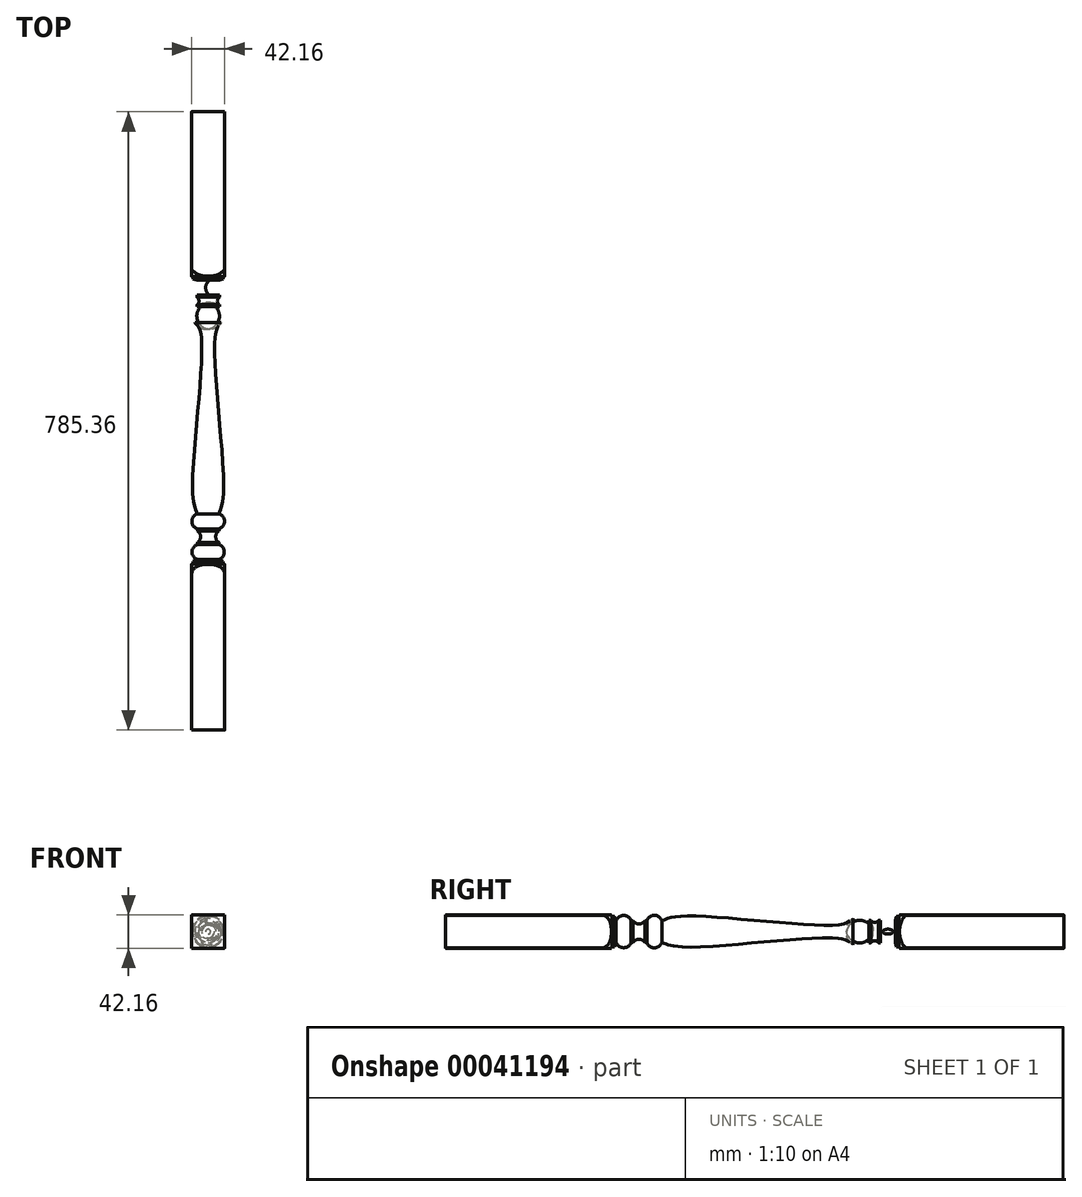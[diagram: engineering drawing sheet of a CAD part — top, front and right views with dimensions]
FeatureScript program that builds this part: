
annotation { "Feature Type Name" : "Feature", "Feature Type Description" : "" }
export const myFeature = defineFeature(function(context is Context, id is Id, definition is map)
    precondition{}
    {
        {
            var Q0;
            Q0=qCreatedBy(makeId("Right.planeOp"),FACE);
            var sketch = newSketch(context, id + "F0", { "sketchPlane" : qUnion([Q0])});
            skLineSegment(sketch, "E0", {"start": v(-252.74, 13.28) * mm, "end": v(-54.81, 13.28) * mm});
            skArc(sketch, "E1", {"start": v(-54.81, 13.28) * mm, "mid": v(-46.4, 16.2) * mm, "end": v(-41.6, 23.69) * mm});
            skLineSegment(sketch, "E2", {"start": v(-41.6, 23.69) * mm, "end": v(-38.43, 23.69) * mm});
            skLineSegment(sketch, "E3", {"start": v(-38.43, 23.69) * mm, "end": v(-36.14, 29.21) * mm});
            skArc(sketch, "E4", {"start": v(-36.14, 29.21) * mm, "mid": v(-26.62, 22.43) * mm, "end": v(-17.1, 29.21) * mm});
            skLineSegment(sketch, "E5", {"start": v(0.3, 29.21) * mm, "end": v(2.84, 29.21) * mm});
            skArc(sketch, "E6", {"start": v(2.84, 29.21) * mm, "mid": v(12.37, 22.22) * mm, "end": v(21.9, 29.21) * mm});
            skArc(sketch, "E7", {"start": v(264.65, 26.2) * mm, "mid": v(275.23, 23.95) * mm, "end": v(284.97, 28.64) * mm});
            skLineSegment(sketch, "E8", {"start": v(284.97, 28.64) * mm, "end": v(287.51, 28.64) * mm});
            skLineSegment(sketch, "E9", {"start": v(297.04, 28.64) * mm, "end": v(299.58, 28.64) * mm});
            skArc(sketch, "E10", {"start": v(299.58, 28.64) * mm, "mid": v(309.1, 23.44) * mm, "end": v(318.63, 28.64) * mm});
            skLineSegment(sketch, "E11", {"start": v(318.63, 28.64) * mm, "end": v(319.9, 23.69) * mm});
            skLineSegment(sketch, "E12", {"start": v(319.9, 23.69) * mm, "end": v(323.07, 23.69) * mm});
            skLineSegment(sketch, "E13", {"start": v(332.6, 13.28) * mm, "end": v(532.62, 13.28) * mm});
            skLineSegment(sketch, "E14", {"start": v(-252.74, 42.93) * mm, "end": v(636.26, 42.93) * mm, "construction": true});
            skLineSegment(sketch, "E15", {"start": v(-17.1, 29.21) * mm, "end": v(-14.55, 29.21) * mm});
            skArc(sketch, "E16", {"start": v(323.07, 23.69) * mm, "mid": v(326.67, 17.42) * mm, "end": v(332.6, 13.28) * mm});
            skLineSegment(sketch, "E17", {"start": v(38.25, 23.05) * mm, "end": v(191.9, 23.05) * mm, "construction": true});
            skFitSpline(sketch, "E18", {"points": [v(21.9, 29.21) * mm, v(52.9, 23.05) * mm, v(249.18, 33.93) * mm, v(264.65, 26.2) * mm], "startDerivative": vector(83.71, -33.8) * mm, "endDerivative": vector(63.68, -47.75) * mm});
            skLineSegment(sketch, "E19.0", {"start": v(-278.65, -33.84) * mm, "end": v(508.75, -33.84) * mm});
            skLineSegment(sketch, "E20", {"start": v(532.62, 13.28) * mm, "end": v(532.62, 42.93) * mm});
            skLineSegment(sketch, "E21", {"start": v(532.62, 42.93) * mm, "end": v(659.62, 42.93) * mm});
            skLineSegment(sketch, "E22", {"start": v(659.62, 42.93) * mm, "end": v(659.62, -33.84) * mm});
            skLineSegment(sketch, "E23", {"start": v(659.62, -33.84) * mm, "end": v(508.75, -33.84) * mm});
            skLineSegment(sketch, "E24", {"start": v(-252.74, 13.28) * mm, "end": v(-252.74, 42.93) * mm});
            skLineSegment(sketch, "E25", {"start": v(-252.74, 42.93) * mm, "end": v(-379.74, 42.93) * mm});
            skLineSegment(sketch, "E26", {"start": v(-379.74, 42.93) * mm, "end": v(-379.74, -33.84) * mm});
            skLineSegment(sketch, "E27", {"start": v(-379.74, -33.84) * mm, "end": v(-278.65, -33.84) * mm});
            skArc(sketch, "E28", {"start": v(0.3, 29.21) * mm, "mid": v(-7.13, 33.3) * mm, "end": v(-14.55, 29.21) * mm});
            skArc(sketch, "E29", {"start": v(297.04, 28.64) * mm, "mid": v(292.28, 31.3) * mm, "end": v(287.51, 28.64) * mm});
            skSolve(sketch);
        }
        {
            var Q0;
            Q0=qCreatedBy(makeId("Front.planeOp"),FACE);
            var sketch = newSketch(context, id + "F1", { "sketchPlane" : qUnion([Q0])});
            skPoint(sketch, "E30.0", {"position": v(0, 42.93) * mm});
            skLineSegment(sketch, "E31.0", {"start": v(-21.08, 21.85) * mm, "end": v(21.08, 21.85) * mm});
            skLineSegment(sketch, "E32.0", {"start": v(-21.08, 64.01) * mm, "end": v(21.08, 64.01) * mm});
            skLineSegment(sketch, "E33.0", {"start": v(21.08, 21.85) * mm, "end": v(21.08, 64.01) * mm});
            skLineSegment(sketch, "E34.0", {"start": v(-21.08, 21.85) * mm, "end": v(-21.08, 64.01) * mm});
            skSolve(sketch);
        }
        {
            var Q0;
            Q0=makeQuery(id+"F1.imprint","IMPRINT",FACE,{"disambiguationData":[TD([[makeQuery(id+"F1.imprint","IMPRINT",EDGE,{"derivedFrom":sQuery(id+"F1.wireOp",EDGE,"E31.0")}),1.0]])]});
            extrude(context, id + "F2", {"entities" : qUnion([Q0]), "depth" : 329.3 * mm});
        }
        {
            var Q0;
            Q0=makeQuery(id+"F2.opExtrude","CAP_FACE",FACE,{"disambiguationData":[OSD([sQuery(id+"F1.wireOp",EDGE,"E31.0"),sQuery(id+"F1.wireOp",EDGE,"E32.0"),sQuery(id+"F1.wireOp",EDGE,"E33.0"),sQuery(id+"F1.wireOp",EDGE,"E34.0")])],"isStart":true});
            extrude(context, id + "F3", {"entities" : qUnion([Q0]), "operationType" : NewBodyOperationType.ADD, "depth" : 569.35 * mm});
        }
        {
            var Q0;
            Q0=makeQuery(id+"F0.imprint","IMPRINT",FACE,{"disambiguationData":[TD([[makeQuery(id+"F0.imprint","IMPRINT",EDGE,{"derivedFrom":sQuery(id+"F0.wireOp",EDGE,"E0")}),-1.0]])]});
            var Q1;
            Q1=sQuery(id+"F0.wireOp",EDGE,"E14");
            revolve(context, id + "F4", {"operationType" : NewBodyOperationType.REMOVE, "entities" : qUnion([Q0]), "axis" : qUnion([Q1]), "revolveType" : RevolveType.FULL, "oppositeDirection" : true});
        }
    });
